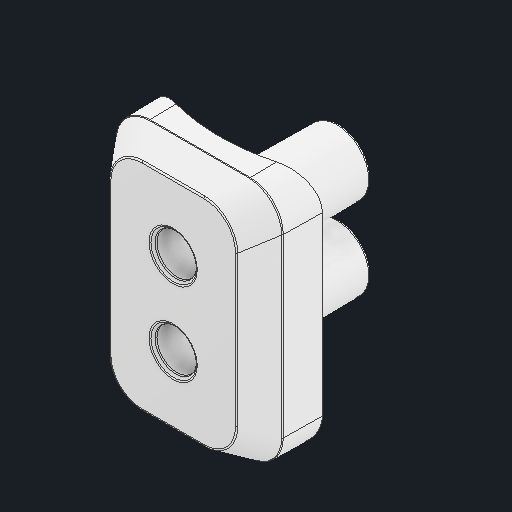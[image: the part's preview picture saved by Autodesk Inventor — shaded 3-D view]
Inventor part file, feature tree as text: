
AUTODESK INVENTOR PART (.ipt)
format: ipt  version: 2024 (Build 280153000, 153)  size: 1,794,560 bytes
history: native  units: in
note: dims shown in document units (in); Inventor stores cm internally (conversion verified against a paired STEP export)
features: fillet x1
ambient origin geometry x8: Origin, YZ Plane, XZ Plane, XY Plane, X Axis, Y Axis, Z Axis, Center Point
bodies: Solid1 (feature_tree)
feature tree (1):
  fillet  "Fillet8"  [1 undecoded]
note: 1 required parameter value undecoded (feature->parameter linkage not recoverable at this tier; creation-order binding heuristic only, values carry confidence <= 0.55)
